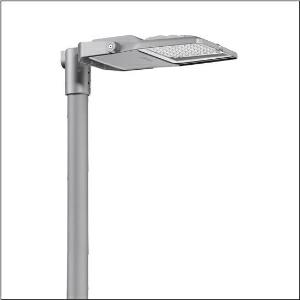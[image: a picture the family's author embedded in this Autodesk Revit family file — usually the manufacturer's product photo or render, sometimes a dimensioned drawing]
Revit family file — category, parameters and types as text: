
# Revit family: floodlight_fl_21_iq_mini___pl64_5xa7772c4e3a_b66a
name_source: partatom
category: Lighting Fixtures
units: mm (PartAtom-declared; Revit-internal decimal feet)

## family parameters
Cut with Voids When Loaded = No
Host = Face
Light Source = No
Part Type = Normal
Room Calculation Point = No
Round Connector Dimension = Use Diameter
Shared = No

## types (1)
- --- (1 x LED, 12280 lm, 87.2 W, 4000K)
    Apparent Load = 87 VA
    CIE Flux Codes = 28 80 98 100 100
    Color Rendering = 70
    Color Temperature = 4000K
    Default Elevation = 1800 mm
    Description = Floodlight FL 21 iQ mini, floodlight, primary light control with lens, of PMMA, primary optical cover: protective disc, of toughened safety glass, transparent, light distribution: PL64, light emission: direct distribution, installation type: surface-mounted, LED, High Power LED, rated luminous flux: 12.280lm, luminous efficacy: 141lm/W, light colour: 740, colour temperature: 4000K, control: Auto-Match, Temp-Guard, Night-Set, Smart-Wire, Desk-Remote (wireless, voltage-free reading and setting of iQ features in the workshop via application-optimized NFC function/RFID function), optimised constant luminous flux control (CLO 2.0), Light-Fading, Lumen-Switch, with terminal, 6-pole, mains connection: 220..240V, AC, 50/60Hz, start of lifetime: 87W, end of service life: 92W, reduction: 40W, luminaire housing, of diecast aluminium, powder-coated, Siteco® metallic grey (DB 702S), corrosivity category C5 mid according to DIN EN ISO 12944, sealing non-destructively replaceable, please order mast flange separately, mast bracket, of steel, galvanised, powder-coated, protection rating (complete): IP66, insulation class (complete): insulation class II (safety insulation), certification: CE, ENEC, VDE, protection symbol: D, impact resistance: IK08, permissible operating ambient temperature: -40..+40°C, permissible operating ambient temperature for outdoor applications: -40..+50°C, standard: DIN EN 12944, LABS conformity tested according to VDMA 24364:2018-05, packaging unit: 1 piece

Light Distribution: PL64
    Height = 70 mm
    Lamp = 1 x LED
    Lamp Light Flux = 12280 lm
    Lamp Power = 87.2 W
    Lamp count = 1
    Length = 485 mm
    Luminous efficacy = 141 lm/W
    Manufacturer = Siteco
    ModVariant = No
    Model = 5XA7772C4E3A
    Number of Poles = 1
    OnlyDefault = Yes
    Power Factor = 1
    Product Name = Floodlight FL 21 iQ mini | PL64
    Product group = floodlight | pylon annexe
    ProductGroupID = 6200
    Protection Class = Protection class II
    Protection Degree = IP 66
    RLX_Detail_Level = 1
    RLX_Emergency_Light_Flux = 0 lm
    RLX_Emergency_Type = 0
    RLX_Emergency_Type_DB = No
    RlxData = <blob elided: 101265 chars, md5=0d0c8aa0>
    Socket = socket
    Standby Power = 0 W
    System Light Flux = 12280 lm
    System Power = 87 W
    Type Comments = factory setting: luminous flux: 100 % | dim-lin: 254 | 456 mA
    Type Image = l_1007125.jpg
    URL = http://relux.com
    VarID = @adj_136551
    Voltage = 0 V
    Weight = 0.00 kg
    Width = 337 mm

## geometry (parser evidence)
native form markers: Blend x4, Sweep x12
no freeform markers — native parametric forms only
